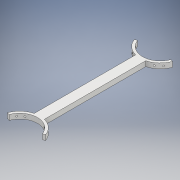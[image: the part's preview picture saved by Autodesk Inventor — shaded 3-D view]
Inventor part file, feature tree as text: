
AUTODESK INVENTOR PART (.ipt)
format: ipt  version: 2017 (Build 210142000, 142)  size: 196,096 bytes
history: native  units: mm
features: sketch x10, plane x8, hole x8, extrude x1, projected_geometry x1
ambient origin geometry x8: Origin, YZ Plane, XZ Plane, XY Plane, X Axis, Y Axis, Z Axis, Center Point
bodies: Solid1 (feature_tree)
feature tree (28):
  extrude  "Extrusion1"  Depth=5.0mm
  sketch  "Sketch2"  dims[d4=27.925268mm d5=200.0mm]
  plane  "Work Plane1"
  plane  "Work Plane2"
  plane  "Work Plane3"
  plane  "Work Plane4"
  plane  "Work Plane5"
  plane  "Work Plane6"
  plane  "Work Plane7"
  plane  "Work Plane8"
  sketch  "Sketch3"  dims[d6=10.0mm d7=0.0mm d8=9.986774mm]
  sketch  "Sketch4"  dims[d9=6.684611mm d10=5.0mm]
  sketch  "Sketch5"  dims[d11=5.0mm d12=5.0mm]
  sketch  "Sketch6"  dims[d13=5.0mm d14=5.0mm]
  sketch  "Sketch8"  dims[d15=5.0mm d16=5.0mm]
  sketch  "Sketch9"  dims[d17=5.0mm]
  sketch  "Sketch10"  dims[d18=3.0mm d19=6.0mm d20=4.0mm d21=2.0mm d22=90.0deg d23=8.0mm d24=20.594885mm]
  sketch  "Sketch11"  dims[d25=3.0mm d26=6.0mm d27=4.0mm d28=2.0mm d29=90.0deg d30=8.0mm d31=20.594885mm d32=3.0mm d33=6.0mm d34=4.0mm d35=2.0mm d36=90.0deg d37=8.0mm d38=20.594885mm d39=3.0mm d40=6.0mm d41=4.0mm d42=2.0mm d43=90.0deg d44=8.0mm d45=20.594885mm d46=3.0mm d47=6.0mm d48=4.0mm d49=2.0mm d50=90.0deg d51=8.0mm d52=20.594885mm d53=3.0mm d54=6.0mm d55=4.0mm d56=2.0mm d57=90.0deg d58=8.0mm d59=20.594885mm d60=3.0mm d61=6.0mm d62=4.0mm d63=2.0mm d64=90.0deg d65=8.0mm d66=20.594885mm d67=3.0mm d68=6.0mm d69=4.0mm d70=2.0mm d71=90.0deg d72=8.0mm d73=20.594885mm]
  hole  "Hole1"  [1 undecoded]
  hole  "Hole2"  [1 undecoded]
  hole  "Hole3"  [1 undecoded]
  hole  "Hole4"  [1 undecoded]
  hole  "Hole5"  [1 undecoded]
  hole  "Hole6"  [1 undecoded]
  hole  "Hole7"  [1 undecoded]
  hole  "Hole8"  [1 undecoded]
  sketch  "Sketch1"  dims[d0=20.0mm d2=5.0mm d3=70.0mm]
  projected_geometry  "Projected Loop1"
note: 8 required parameter values undecoded (feature->parameter linkage not recoverable at this tier; creation-order binding heuristic only, values carry confidence <= 0.55)
